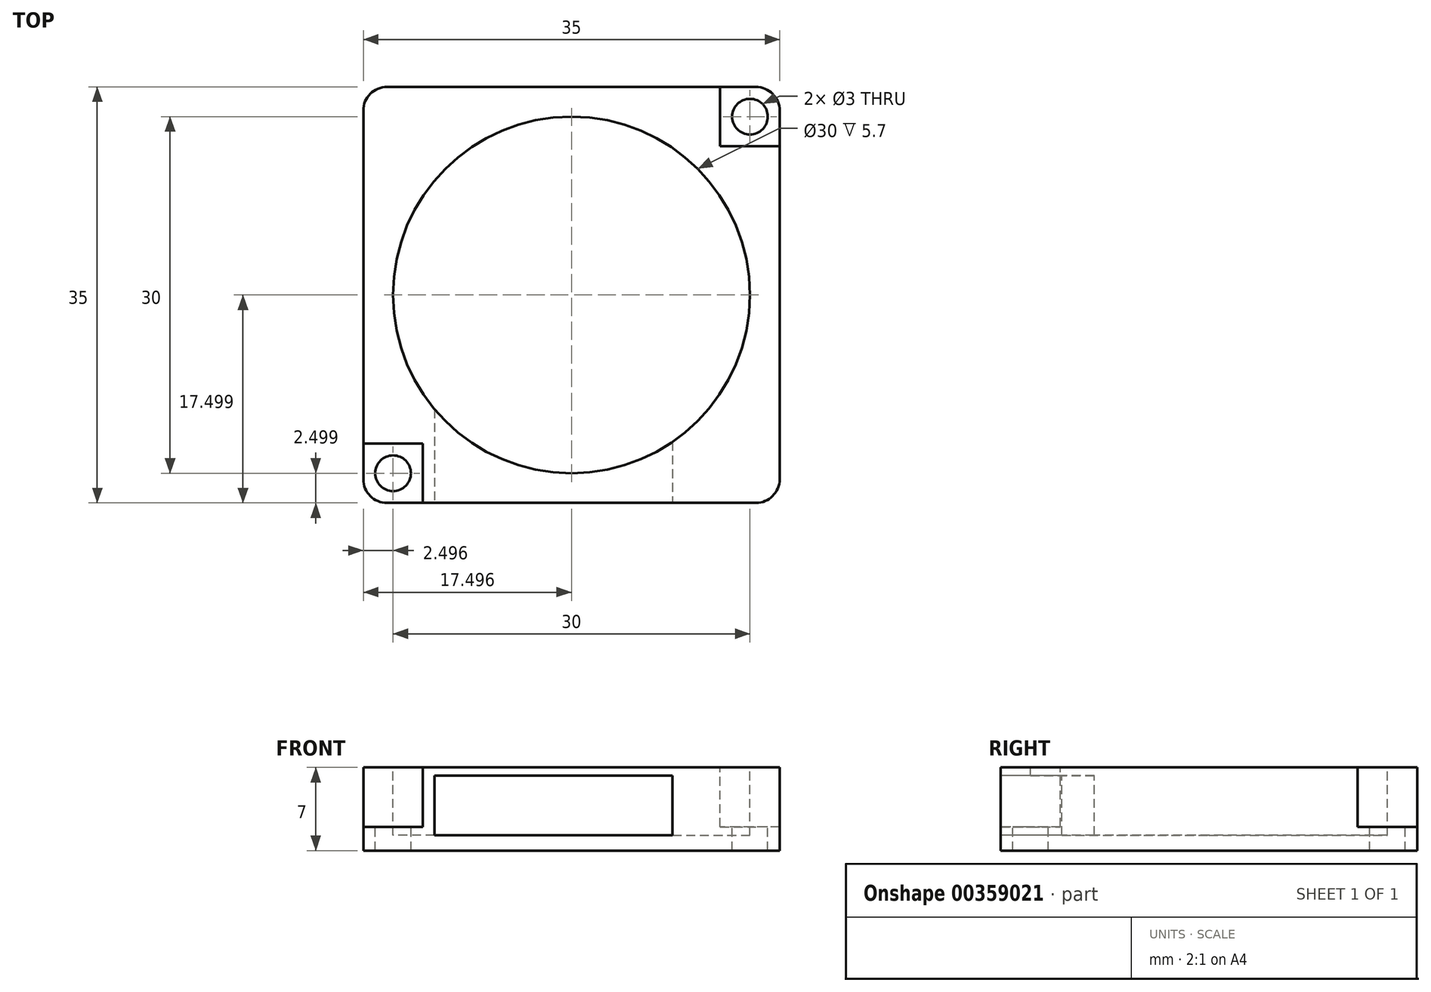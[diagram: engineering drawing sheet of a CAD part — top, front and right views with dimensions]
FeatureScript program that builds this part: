
annotation { "Feature Type Name" : "Feature", "Feature Type Description" : "" }
export const myFeature = defineFeature(function(context is Context, id is Id, definition is map)
    precondition{}
    {
        {
            var Q0;
            Q0=qCreatedBy(makeId("Top.planeOp"),FACE);
            var sketch = newSketch(context, id + "F0", { "sketchPlane" : qUnion([Q0])});
            skLineSegment(sketch, "E0.bottom", {"start": v(-26.56, 16.37) * mm, "end": v(8.44, 16.37) * mm});
            skLineSegment(sketch, "E0.top", {"start": v(-26.56, -18.63) * mm, "end": v(8.44, -18.63) * mm});
            skLineSegment(sketch, "E0.left", {"start": v(-26.56, 16.37) * mm, "end": v(-26.56, -18.63) * mm});
            skLineSegment(sketch, "E0.right", {"start": v(8.44, 16.37) * mm, "end": v(8.44, -18.63) * mm});
            skSolve(sketch);
        }
        {
            var Q0;
            Q0=makeQuery(id+"F0.imprint","IMPRINT",FACE,{"disambiguationData":[TD([[makeQuery(id+"F0.imprint","IMPRINT",EDGE,{"derivedFrom":sQuery(id+"F0.wireOp",EDGE,"E0.bottom")}),-1.0]])]});
            extrude(context, id + "F1", {"entities" : qUnion([Q0]), "depth" : 7 * mm});
        }
        {
            var Q0;
            Q0=makeQuery(id+"F1.opExtrude","CAP_FACE",FACE,{"disambiguationData":[OSD([sQuery(id+"F0.wireOp",EDGE,"E0.bottom"),sQuery(id+"F0.wireOp",EDGE,"E0.top"),sQuery(id+"F0.wireOp",EDGE,"E0.left"),sQuery(id+"F0.wireOp",EDGE,"E0.right")])],"isStart":false});
            var sketch = newSketch(context, id + "F2", { "sketchPlane" : qUnion([Q0])});
            skLineSegment(sketch, "E1.bottom", {"start": v(-26.56, -18.63) * mm, "end": v(-21.56, -18.63) * mm});
            skLineSegment(sketch, "E1.top", {"start": v(-26.56, -13.63) * mm, "end": v(-21.56, -13.63) * mm});
            skLineSegment(sketch, "E1.left", {"start": v(-26.56, -18.63) * mm, "end": v(-26.56, -13.63) * mm});
            skLineSegment(sketch, "E1.right", {"start": v(-21.56, -18.63) * mm, "end": v(-21.56, -13.63) * mm});
            skLineSegment(sketch, "E2.bottom", {"start": v(8.44, 16.37) * mm, "end": v(3.44, 16.37) * mm});
            skLineSegment(sketch, "E2.top", {"start": v(8.44, 11.37) * mm, "end": v(3.44, 11.37) * mm});
            skLineSegment(sketch, "E2.left", {"start": v(8.44, 16.37) * mm, "end": v(8.44, 11.37) * mm});
            skLineSegment(sketch, "E2.right", {"start": v(3.44, 16.37) * mm, "end": v(3.44, 11.37) * mm});
            skSolve(sketch);
        }
        {
            var Q0;
            Q0=makeQuery(id+"F2.imprint","IMPRINT",FACE,{"disambiguationData":[TD([[makeQuery(id+"F2.imprint","IMPRINT",EDGE,{"derivedFrom":sQuery(id+"F2.wireOp",EDGE,"E1.bottom")}),1.0]])]});
            var Q1;
            Q1=makeQuery(id+"F2.imprint","IMPRINT",FACE,{"disambiguationData":[TD([[makeQuery(id+"F2.imprint","IMPRINT",EDGE,{"derivedFrom":sQuery(id+"F2.wireOp",EDGE,"E2.bottom")}),-1.0]])]});
            extrude(context, id + "F3", {"entities" : qUnion([Q0, Q1]), "operationType" : NewBodyOperationType.REMOVE, "oppositeDirection" : true, "depth" : 5 * mm});
        }
        {
            var Q0;
            Q0=makeQuery(id+"F1.opExtrude","CAP_FACE",FACE,{"disambiguationData":[OSD([sQuery(id+"F0.wireOp",EDGE,"E0.bottom"),sQuery(id+"F0.wireOp",EDGE,"E0.top"),sQuery(id+"F0.wireOp",EDGE,"E0.left"),sQuery(id+"F0.wireOp",EDGE,"E0.right")])],"isStart":false});
            var sketch = newSketch(context, id + "F4", { "sketchPlane" : qUnion([Q0])});
            skCircle(sketch, "E3", {"center": v(-9.06, -1.13) * mm, "radius": 15 * mm});
            skSolve(sketch);
        }
        {
            var Q0;
            Q0=makeQuery(id+"F4.imprint","IMPRINT",FACE,{"disambiguationData":[TD([[makeQuery(id+"F4.imprint","IMPRINT",EDGE,{"derivedFrom":sQuery(id+"F4.wireOp",EDGE,"E3")}),1.0]])]});
            extrude(context, id + "F5", {"entities" : qUnion([Q0]), "operationType" : NewBodyOperationType.REMOVE, "oppositeDirection" : true, "depth" : 5.7 * mm});
        }
        {
            var Q0;
            Q0=makeQuery(id+"F3.boolean.opBoolean","COPY",FACE,{"derivedFrom":makeQuery(id+"F3.opExtrude","CAP_FACE",FACE,{"disambiguationData":[OSD([sQuery(id+"F2.wireOp",EDGE,"E2.bottom"),sQuery(id+"F2.wireOp",EDGE,"E2.top"),sQuery(id+"F2.wireOp",EDGE,"E2.left"),sQuery(id+"F2.wireOp",EDGE,"E2.right")])],"isStart":false})});
            var sketch = newSketch(context, id + "F6", { "sketchPlane" : qUnion([Q0])});
            skCircle(sketch, "E4", {"center": v(5.94, 13.87) * mm, "radius": 1.5 * mm});
            skCircle(sketch, "E5", {"center": v(-24.06, -16.13) * mm, "radius": 1.5 * mm});
            skSolve(sketch);
        }
        {
            var Q0;
            Q0=makeQuery(id+"F6.imprint","IMPRINT",FACE,{"disambiguationData":[TD([[makeQuery(id+"F6.imprint","IMPRINT",EDGE,{"derivedFrom":sQuery(id+"F6.wireOp",EDGE,"E5")}),1.0]])]});
            var Q1;
            Q1=makeQuery(id+"F6.imprint","IMPRINT",FACE,{"disambiguationData":[TD([[makeQuery(id+"F6.imprint","IMPRINT",EDGE,{"derivedFrom":sQuery(id+"F6.wireOp",EDGE,"E4")}),1.0]])]});
            extrude(context, id + "F7", {"entities" : qUnion([Q0, Q1]), "operationType" : NewBodyOperationType.REMOVE, "oppositeDirection" : true, "depth" : 25 * mm});
        }
        {
            var Q0;
            Q0=makeQuery(id+"F1.opExtrude","SWEPT_FACE",FACE,{"disambiguationData":[OSD([sQuery(id+"F0.wireOp",EDGE,"E0.top")])]});
            var sketch = newSketch(context, id + "F8", { "sketchPlane" : qUnion([Q0])});
            skLineSegment(sketch, "E6.bottom", {"start": v(-20.56, 6.3) * mm, "end": v(-0.56, 6.3) * mm});
            skLineSegment(sketch, "E6.top", {"start": v(-20.56, 1.3) * mm, "end": v(-0.56, 1.3) * mm});
            skLineSegment(sketch, "E6.left", {"start": v(-20.56, 6.3) * mm, "end": v(-20.56, 1.3) * mm});
            skLineSegment(sketch, "E6.right", {"start": v(-0.56, 6.3) * mm, "end": v(-0.56, 1.3) * mm});
            skSolve(sketch);
        }
        {
            var Q0;
            Q0=makeQuery(id+"F8.imprint","IMPRINT",FACE,{"disambiguationData":[TD([[makeQuery(id+"F8.imprint","IMPRINT",EDGE,{"derivedFrom":sQuery(id+"F8.wireOp",EDGE,"E6.bottom")}),-1.0]])]});
            extrude(context, id + "F9", {"entities" : qUnion([Q0]), "operationType" : NewBodyOperationType.REMOVE, "oppositeDirection" : true, "depth" : 10 * mm});
        }
        {
            var Q0;
            Q0=makeQuery(id+"F1.opExtrude","SWEPT_EDGE",EDGE,{"disambiguationData":[OSD([sQuery(id+"F0.wireOp",EDGE,"E0.top"),sQuery(id+"F0.wireOp",EDGE,"E0.right")])]});
            var Q1;
            Q1=makeQuery(id+"F1.opExtrude","SWEPT_EDGE",EDGE,{"disambiguationData":[OSD([sQuery(id+"F0.wireOp",EDGE,"E0.top"),sQuery(id+"F0.wireOp",EDGE,"E0.left")])]});
            var Q2;
            Q2=makeQuery(id+"F1.opExtrude","SWEPT_EDGE",EDGE,{"disambiguationData":[OSD([sQuery(id+"F0.wireOp",EDGE,"E0.bottom"),sQuery(id+"F0.wireOp",EDGE,"E0.right")])]});
            var Q3;
            Q3=makeQuery(id+"F1.opExtrude","SWEPT_EDGE",EDGE,{"disambiguationData":[OSD([sQuery(id+"F0.wireOp",EDGE,"E0.bottom"),sQuery(id+"F0.wireOp",EDGE,"E0.left")])]});
            fillet(context, id + "F10", {"entities" : qUnion([Q0, Q1, Q2, Q3]), "radius" : 2 * mm, "tangentPropagation" : true, "allowEdgeOverflow" : false});
        }
    });
